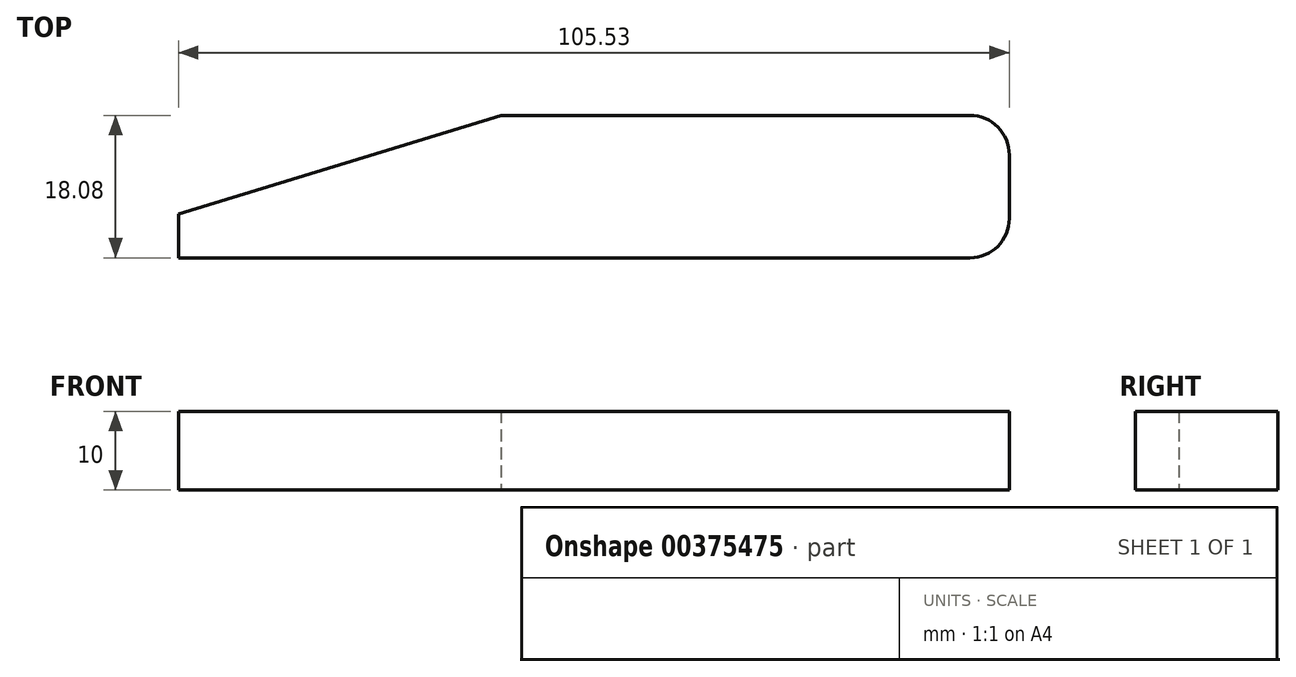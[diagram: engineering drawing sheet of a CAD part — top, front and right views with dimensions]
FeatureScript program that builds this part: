
annotation { "Feature Type Name" : "Feature", "Feature Type Description" : "" }
export const myFeature = defineFeature(function(context is Context, id is Id, definition is map)
    precondition{}
    {
        {
            var Q0;
            Q0=qCreatedBy(makeId("Top.planeOp"),FACE);
            var sketch = newSketch(context, id + "F0", { "sketchPlane" : qUnion([Q0])});
            skLineSegment(sketch, "E0.bottom", {"start": v(0, 0) * mm, "end": v(-64.57, 0) * mm});
            skLineSegment(sketch, "E0.top", {"start": v(0, 18.08) * mm, "end": v(-64.57, 18.08) * mm});
            skLineSegment(sketch, "E0.left", {"start": v(0, 0) * mm, "end": v(0, 18.08) * mm});
            skLineSegment(sketch, "E1", {"start": v(-64.57, 0) * mm, "end": v(-105.53, 0) * mm});
            skLineSegment(sketch, "E2", {"start": v(-105.53, 0) * mm, "end": v(-105.53, 5.53) * mm});
            skLineSegment(sketch, "E3", {"start": v(-105.53, 5.53) * mm, "end": v(-64.57, 18.08) * mm});
            skSolve(sketch);
        }
        {
            var Q0;
            Q0=makeQuery(id+"F0.imprint","IMPRINT",FACE,{"disambiguationData":[TD([[makeQuery(id+"F0.imprint","IMPRINT",EDGE,{"derivedFrom":sQuery(id+"F0.wireOp",EDGE,"E0.bottom")}),-1.0]])]});
            extrude(context, id + "F1", {"entities" : qUnion([Q0]), "depth" : 10 * mm});
        }
        {
            var Q0;
            Q0=makeQuery(id+"F1.opExtrude","SWEPT_EDGE",EDGE,{"disambiguationData":[OSD([sQuery(id+"F0.wireOp",EDGE,"E0.top"),sQuery(id+"F0.wireOp",EDGE,"E0.left")])]});
            var Q1;
            Q1=makeQuery(id+"F1.opExtrude","SWEPT_EDGE",EDGE,{"disambiguationData":[OSD([sQuery(id+"F0.wireOp",EDGE,"E0.bottom"),sQuery(id+"F0.wireOp",EDGE,"E0.left")])]});
            fillet(context, id + "F2", {"entities" : qUnion([Q0, Q1]), "radius" : 5 * mm, "tangentPropagation" : true, "allowEdgeOverflow" : false});
        }
    });
